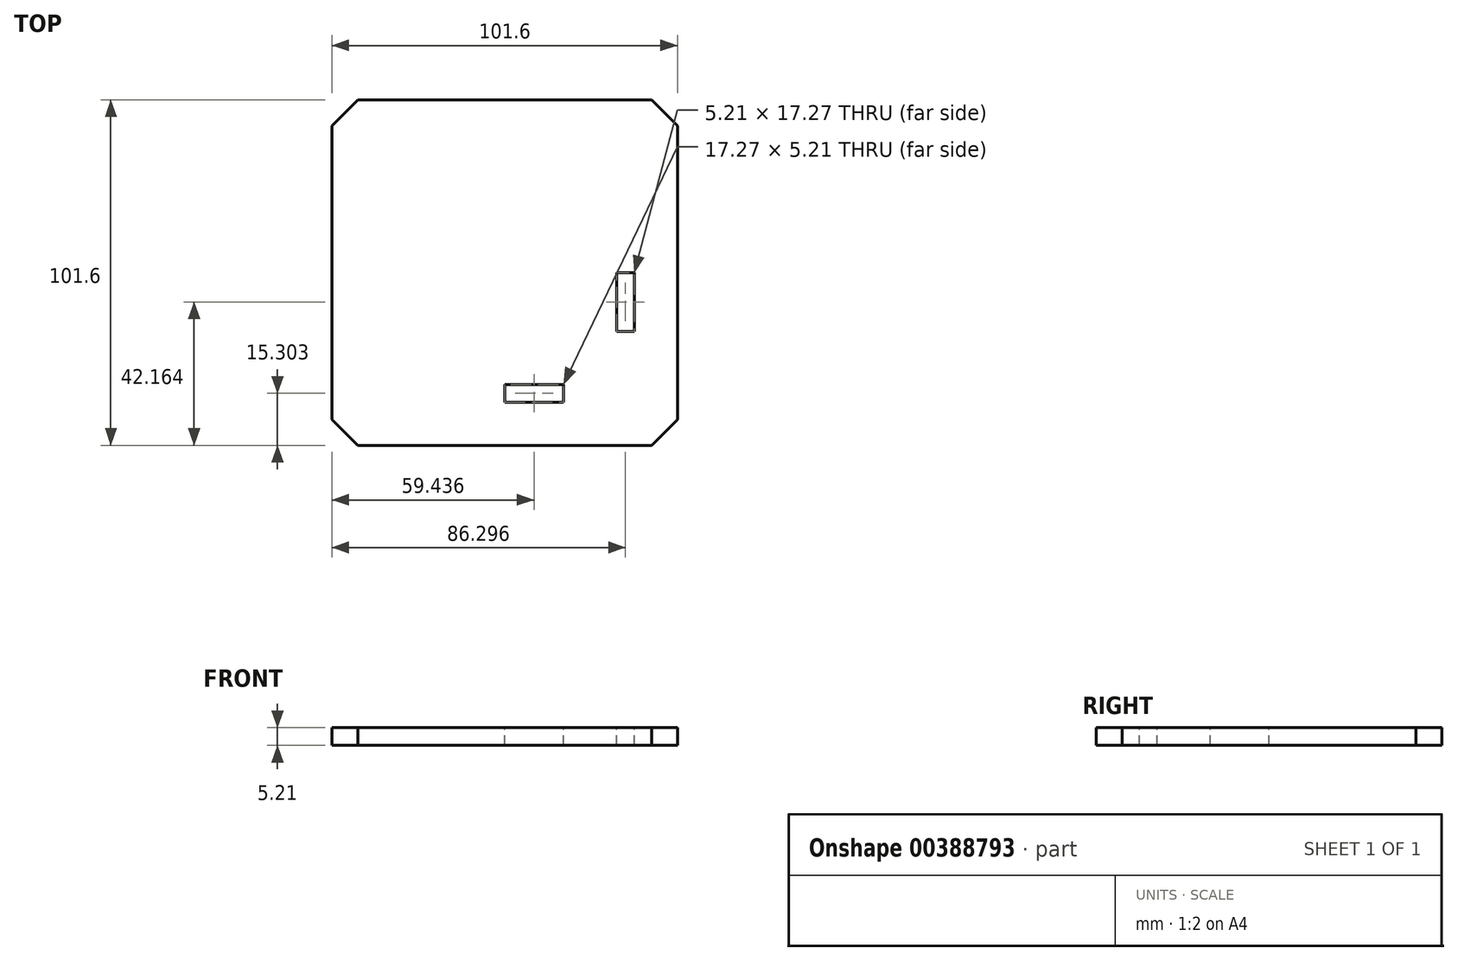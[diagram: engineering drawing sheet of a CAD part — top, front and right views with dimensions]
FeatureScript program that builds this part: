
annotation { "Feature Type Name" : "Feature", "Feature Type Description" : "" }
export const myFeature = defineFeature(function(context is Context, id is Id, definition is map)
    precondition{}
    {
        {
            var Q0;
            Q0=qCreatedBy(makeId("Top.planeOp"),FACE);
            var sketch = newSketch(context, id + "F0", { "sketchPlane" : qUnion([Q0])});
            skLineSegment(sketch, "E0.bottom", {"start": v(50.8, -50.8) * mm, "end": v(-50.8, -50.8) * mm});
            skLineSegment(sketch, "E0.top", {"start": v(50.8, 50.8) * mm, "end": v(-50.8, 50.8) * mm});
            skLineSegment(sketch, "E0.left", {"start": v(50.8, -50.8) * mm, "end": v(50.8, 50.8) * mm});
            skLineSegment(sketch, "E0.right", {"start": v(-50.8, -50.8) * mm, "end": v(-50.8, 50.8) * mm});
            skPoint(sketch, "E0.middle", {"position": v(0, 0) * mm});
            skSolve(sketch);
        }
        {
            var Q0;
            Q0=qSketchRegion(id+"F0",true);
            extrude(context, id + "F1", {"entities" : qUnion([Q0]), "depth" : 5.2 * mm});
        }
        {
            var Q0;
            Q0=makeQuery(id+"F1.opExtrude","SWEPT_EDGE",EDGE,{"disambiguationData":[OSD([sQuery(id+"F0.wireOp",EDGE,"E0.bottom"),sQuery(id+"F0.wireOp",EDGE,"E0.left")])]});
            var Q1;
            Q1=makeQuery(id+"F1.opExtrude","SWEPT_EDGE",EDGE,{"disambiguationData":[OSD([sQuery(id+"F0.wireOp",EDGE,"E0.bottom"),sQuery(id+"F0.wireOp",EDGE,"E0.right")])]});
            var Q2;
            Q2=makeQuery(id+"F1.opExtrude","SWEPT_EDGE",EDGE,{"disambiguationData":[OSD([sQuery(id+"F0.wireOp",EDGE,"E0.top"),sQuery(id+"F0.wireOp",EDGE,"E0.left")])]});
            var Q3;
            Q3=makeQuery(id+"F1.opExtrude","SWEPT_EDGE",EDGE,{"disambiguationData":[OSD([sQuery(id+"F0.wireOp",EDGE,"E0.top"),sQuery(id+"F0.wireOp",EDGE,"E0.right")])]});
            chamfer(context, id + "F2", {"entities" : qUnion([Q0, Q1, Q2, Q3]), "width" : 7.62 * mm, "tangentPropagation" : true});
        }
        {
            var Q0;
            Q0=makeQuery(id+"F1.opExtrude","CAP_FACE",FACE,{"disambiguationData":[OSD([sQuery(id+"F0.wireOp",EDGE,"E0.bottom"),sQuery(id+"F0.wireOp",EDGE,"E0.top"),sQuery(id+"F0.wireOp",EDGE,"E0.left"),sQuery(id+"F0.wireOp",EDGE,"E0.right")])],"isStart":false});
            var sketch = newSketch(context, id + "F3", { "sketchPlane" : qUnion([Q0])});
            skLineSegment(sketch, "E1.bottom", {"start": v(38.1, -38.1) * mm, "end": v(-38.1, -38.1) * mm});
            skLineSegment(sketch, "E1.top", {"start": v(38.1, 38.1) * mm, "end": v(-38.1, 38.1) * mm});
            skLineSegment(sketch, "E1.left", {"start": v(38.1, -38.1) * mm, "end": v(38.1, 38.1) * mm});
            skLineSegment(sketch, "E1.right", {"start": v(-38.1, -38.1) * mm, "end": v(-38.1, 38.1) * mm});
            skPoint(sketch, "E1.middle", {"position": v(0, 0) * mm});
            skLineSegment(sketch, "E2.bottom", {"start": v(32.9, -32.9) * mm, "end": v(-32.9, -32.9) * mm});
            skLineSegment(sketch, "E2.top", {"start": v(32.9, 32.9) * mm, "end": v(-32.9, 32.9) * mm});
            skLineSegment(sketch, "E2.left", {"start": v(32.9, -32.9) * mm, "end": v(32.9, 32.9) * mm});
            skLineSegment(sketch, "E2.right", {"start": v(-32.9, -32.9) * mm, "end": v(-32.9, 32.9) * mm});
            skLineSegment(sketch, "E3", {"start": v(38.1, 0) * mm, "end": v(50.8, 0) * mm});
            skLineSegment(sketch, "E4", {"start": v(0, -38.1) * mm, "end": v(0, -50.8) * mm});
            skLineSegment(sketch, "E5", {"start": v(0, -38.1) * mm, "end": v(0, -32.9) * mm});
            skLineSegment(sketch, "E6", {"start": v(0, -32.9) * mm, "end": v(32.9, 0) * mm});
            skLineSegment(sketch, "E7", {"start": v(32.9, 0) * mm, "end": v(38.1, 0) * mm});
            skLineSegment(sketch, "E8", {"start": v(32.9, -17.27) * mm, "end": v(38.1, -17.27) * mm});
            skLineSegment(sketch, "E9", {"start": v(17.27, -32.9) * mm, "end": v(17.27, -38.1) * mm});
            skSolve(sketch);
        }
        {
            var Q0;
            {var subQ0=sQuery(id+"F3.wireOp",EDGE,"E5");Q0=makeQuery(id+"F3.imprint","IMPRINT",FACE,{"disambiguationData":[TD([[makeQuery(id+"F3.imprint","IMPRINT",EDGE,{"derivedFrom":subQ0}),-1.0]])]});}
            var Q1;
            {var subQ0=sQuery(id+"F3.wireOp",EDGE,"E7");Q1=makeQuery(id+"F3.imprint","IMPRINT",FACE,{"disambiguationData":[TD([[makeQuery(id+"F3.imprint","IMPRINT",EDGE,{"derivedFrom":subQ0}),-1.0]])]});}
            extrude(context, id + "F4", {"entities" : qUnion([Q0, Q1]), "operationType" : NewBodyOperationType.REMOVE, "oppositeDirection" : true, "depth" : 25.4 * mm});
        }
        {
            var Q0;
            Q0=makeQuery(id+"F1.opExtrude","CAP_EDGE",EDGE,{"disambiguationData":[OSD([sQuery(id+"F0.wireOp",EDGE,"E0.bottom")])],"isStart":false});
            cPoint(context, id + "F5", {"entities" : qUnion([Q0]), "parameter" : 0.5});
        }
        {
            var Q0;
            Q0=makeQuery(id+"F1.opExtrude","CAP_EDGE",EDGE,{"disambiguationData":[OSD([sQuery(id+"F0.wireOp",EDGE,"E0.bottom")])],"isStart":true});
            cPoint(context, id + "F6", {"entities" : qUnion([Q0]), "parameter" : 0.5});
        }
        {
            var Q0;
            Q0=makeQuery(id+"F1.opExtrude","CAP_EDGE",EDGE,{"disambiguationData":[OSD([sQuery(id+"F0.wireOp",EDGE,"E0.top")])],"isStart":false});
            cPoint(context, id + "F7", {"entities" : qUnion([Q0]), "parameter" : 0.5});
        }
        {
            var Q0;
            Q0 = qCreatedBy(id + "F5" ,VERTEX);
            var Q1;
            Q1 = qCreatedBy(id + "F6" ,VERTEX);
            var Q2;
            Q2 = qCreatedBy(id + "F7" ,VERTEX);
            cPlane(context, id + "F8", {"entities" : qUnion([Q0, Q1, Q2]), "cplaneType" : CPlaneType.THREE_POINT, "offset" : 25.4 * mm, "width" : 152.4 * mm, "height" : 152.4 * mm});
        }
        {
            var Q0;
            Q0=makeQuery(id+"F1.opExtrude","CAP_EDGE",EDGE,{"disambiguationData":[OSD([sQuery(id+"F0.wireOp",EDGE,"E0.left")])],"isStart":false});
            cPoint(context, id + "F9", {"entities" : qUnion([Q0]), "parameter" : 0.5});
        }
        {
            var Q0;
            Q0=makeQuery(id+"F1.opExtrude","CAP_EDGE",EDGE,{"disambiguationData":[OSD([sQuery(id+"F0.wireOp",EDGE,"E0.left")])],"isStart":true});
            cPoint(context, id + "F10", {"entities" : qUnion([Q0]), "parameter" : 0.5});
        }
        {
            var Q0;
            Q0=makeQuery(id+"F1.opExtrude","CAP_EDGE",EDGE,{"disambiguationData":[OSD([sQuery(id+"F0.wireOp",EDGE,"E0.right")])],"isStart":false});
            cPoint(context, id + "F11", {"entities" : qUnion([Q0]), "parameter" : 0.5});
        }
        {
            var Q0;
            Q0 = qCreatedBy(id + "F9" ,VERTEX);
            var Q1;
            Q1 = qCreatedBy(id + "F10" ,VERTEX);
            var Q2;
            Q2 = qCreatedBy(id + "F11" ,VERTEX);
            cPlane(context, id + "F12", {"entities" : qUnion([Q0, Q1, Q2]), "cplaneType" : CPlaneType.THREE_POINT, "offset" : 25.4 * mm, "width" : 152.4 * mm, "height" : 152.4 * mm});
        }
    });
